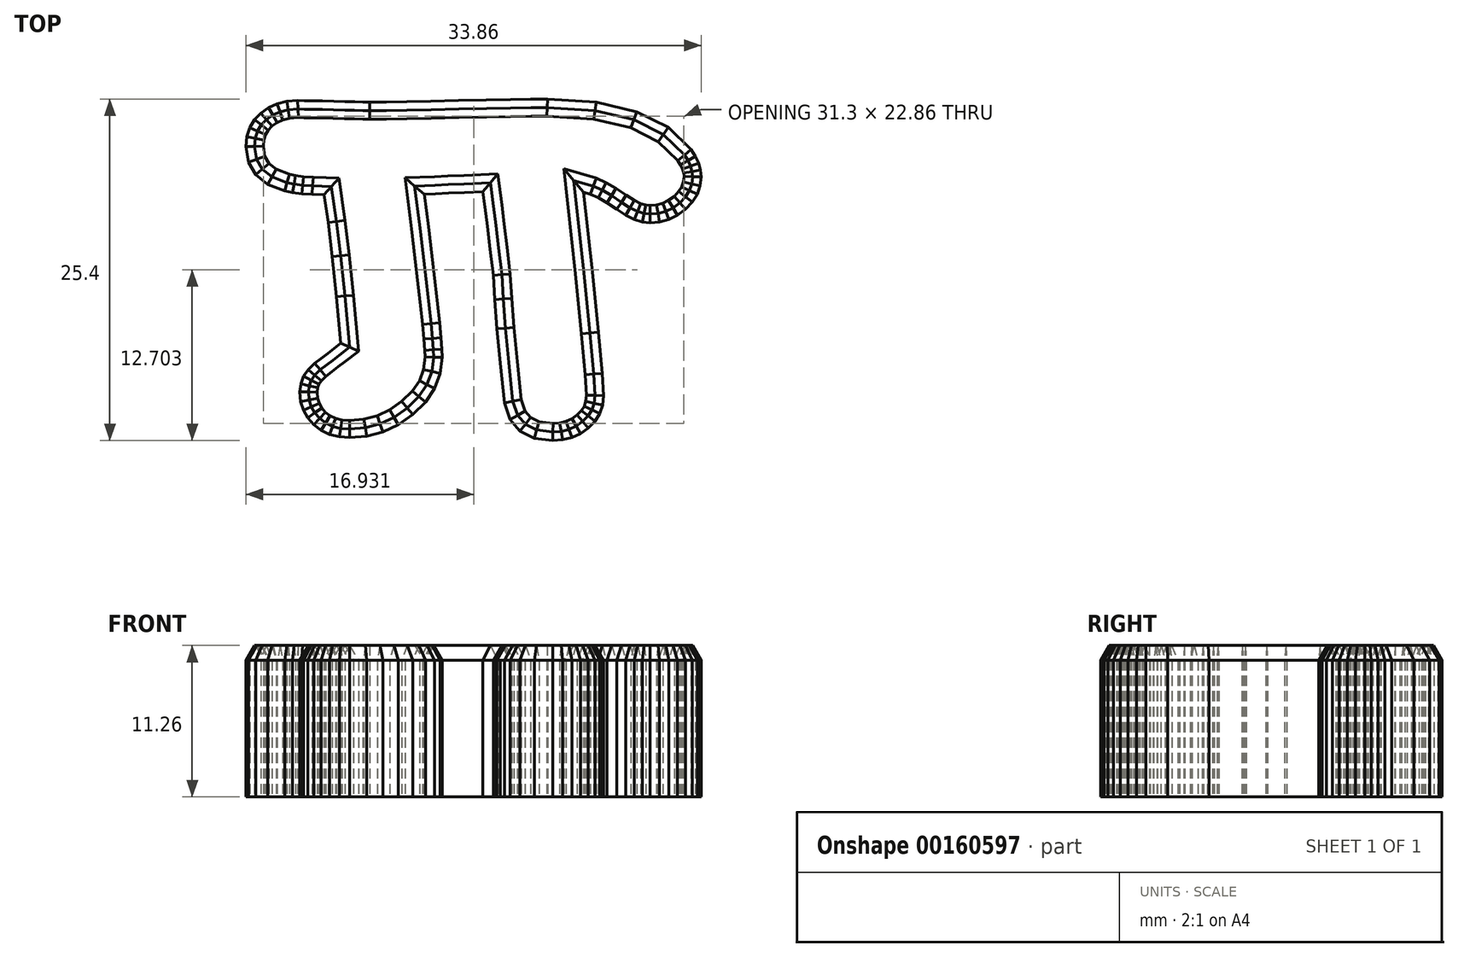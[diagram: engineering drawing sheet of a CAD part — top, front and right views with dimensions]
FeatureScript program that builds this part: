
annotation { "Feature Type Name" : "Feature", "Feature Type Description" : "" }
export const myFeature = defineFeature(function(context is Context, id is Id, definition is map)
    precondition{}
    {
        {
            var Q0;
            Q0=qCreatedBy(makeId("Top.planeOp"),FACE);
            var sketch = newSketch(context, id + "F0", { "sketchPlane" : qUnion([Q0])});
            skLineSegment(sketch, "E0", {"start": v(-14.06, 5.88) * mm, "end": v(-13.47, 5.76) * mm});
            skLineSegment(sketch, "E1", {"start": v(-13.47, 5.76) * mm, "end": v(-12.79, 5.67) * mm});
            skLineSegment(sketch, "E2", {"start": v(-12.79, 5.67) * mm, "end": v(-12, 5.6) * mm});
            skLineSegment(sketch, "E3", {"start": v(-12, 5.6) * mm, "end": v(-11.13, 5.58) * mm});
            skLineSegment(sketch, "E4", {"start": v(-11.13, 5.58) * mm, "end": v(-10.82, 3.51) * mm});
            skLineSegment(sketch, "E5", {"start": v(-10.82, 3.51) * mm, "end": v(-10.51, 0.98) * mm});
            skLineSegment(sketch, "E6", {"start": v(-10.51, 0.98) * mm, "end": v(-10.2, -2.01) * mm});
            skLineSegment(sketch, "E7", {"start": v(-10.2, -2.01) * mm, "end": v(-9.89, -5.47) * mm});
            skLineSegment(sketch, "E8", {"start": v(-9.89, -5.47) * mm, "end": v(-10.37, -5.84) * mm});
            skLineSegment(sketch, "E9", {"start": v(-10.37, -5.84) * mm, "end": v(-10.85, -6.21) * mm});
            skLineSegment(sketch, "E10", {"start": v(-10.85, -6.21) * mm, "end": v(-11.34, -6.59) * mm});
            skLineSegment(sketch, "E11", {"start": v(-11.34, -6.59) * mm, "end": v(-11.82, -6.96) * mm});
            skLineSegment(sketch, "E12", {"start": v(-11.82, -6.96) * mm, "end": v(-12.3, -7.41) * mm});
            skLineSegment(sketch, "E13", {"start": v(-12.3, -7.41) * mm, "end": v(-12.65, -7.92) * mm});
            skLineSegment(sketch, "E14", {"start": v(-12.65, -7.92) * mm, "end": v(-12.86, -8.48) * mm});
            skLineSegment(sketch, "E15", {"start": v(-12.86, -8.48) * mm, "end": v(-12.92, -9.09) * mm});
            skLineSegment(sketch, "E16", {"start": v(-12.92, -9.09) * mm, "end": v(-12.86, -9.8) * mm});
            skLineSegment(sketch, "E17", {"start": v(-12.86, -9.8) * mm, "end": v(-12.67, -10.44) * mm});
            skLineSegment(sketch, "E18", {"start": v(-12.67, -10.44) * mm, "end": v(-12.34, -11.02) * mm});
            skLineSegment(sketch, "E19", {"start": v(-12.34, -11.02) * mm, "end": v(-11.89, -11.53) * mm});
            skLineSegment(sketch, "E20", {"start": v(-11.89, -11.53) * mm, "end": v(-11.33, -11.95) * mm});
            skLineSegment(sketch, "E21", {"start": v(-11.33, -11.95) * mm, "end": v(-10.7, -12.24) * mm});
            skLineSegment(sketch, "E22", {"start": v(-10.7, -12.24) * mm, "end": v(-10, -12.42) * mm});
            skLineSegment(sketch, "E23", {"start": v(-10, -12.42) * mm, "end": v(-9.22, -12.48) * mm});
            skLineSegment(sketch, "E24", {"start": v(-9.22, -12.48) * mm, "end": v(-7.95, -12.38) * mm});
            skLineSegment(sketch, "E25", {"start": v(-7.95, -12.38) * mm, "end": v(-6.74, -12.05) * mm});
            skLineSegment(sketch, "E26", {"start": v(-6.74, -12.05) * mm, "end": v(-5.6, -11.52) * mm});
            skLineSegment(sketch, "E27", {"start": v(-5.6, -11.52) * mm, "end": v(-4.53, -10.77) * mm});
            skLineSegment(sketch, "E28", {"start": v(-4.53, -10.77) * mm, "end": v(-3.57, -9.84) * mm});
            skLineSegment(sketch, "E29", {"start": v(-3.57, -9.84) * mm, "end": v(-2.9, -8.82) * mm});
            skLineSegment(sketch, "E30", {"start": v(-2.9, -8.82) * mm, "end": v(-2.48, -7.72) * mm});
            skLineSegment(sketch, "E31", {"start": v(-2.48, -7.72) * mm, "end": v(-2.35, -6.52) * mm});
            skLineSegment(sketch, "E32", {"start": v(-2.35, -6.52) * mm, "end": v(-2.37, -5.92) * mm});
            skLineSegment(sketch, "E33", {"start": v(-2.37, -5.92) * mm, "end": v(-2.43, -5.05) * mm});
            skLineSegment(sketch, "E34", {"start": v(-2.43, -5.05) * mm, "end": v(-2.53, -3.93) * mm});
            skLineSegment(sketch, "E35", {"start": v(-2.53, -3.93) * mm, "end": v(-2.68, -2.54) * mm});
            skLineSegment(sketch, "E36", {"start": v(-2.68, -2.54) * mm, "end": v(-2.87, -0.9) * mm});
            skLineSegment(sketch, "E37", {"start": v(-2.87, -0.9) * mm, "end": v(-3.1, 1.02) * mm});
            skLineSegment(sketch, "E38", {"start": v(-3.1, 1.02) * mm, "end": v(-3.36, 3.2) * mm});
            skLineSegment(sketch, "E39", {"start": v(-3.36, 3.2) * mm, "end": v(-3.67, 5.63) * mm});
            skLineSegment(sketch, "E40", {"start": v(-3.67, 5.63) * mm, "end": v(-2.85, 5.67) * mm});
            skLineSegment(sketch, "E41", {"start": v(-2.85, 5.67) * mm, "end": v(-1.85, 5.7) * mm});
            skLineSegment(sketch, "E42", {"start": v(-1.85, 5.7) * mm, "end": v(-0.67, 5.76) * mm});
            skLineSegment(sketch, "E43", {"start": v(-0.67, 5.76) * mm, "end": v(0.7, 5.83) * mm});
            skLineSegment(sketch, "E44", {"start": v(0.7, 5.83) * mm, "end": v(0.84, 4.66) * mm});
            skLineSegment(sketch, "E45", {"start": v(0.84, 4.66) * mm, "end": v(1.02, 3.23) * mm});
            skLineSegment(sketch, "E46", {"start": v(1.02, 3.23) * mm, "end": v(1.23, 1.54) * mm});
            skLineSegment(sketch, "E47", {"start": v(1.23, 1.54) * mm, "end": v(1.46, -0.41) * mm});
            skLineSegment(sketch, "E48", {"start": v(1.46, -0.41) * mm, "end": v(1.57, -2.2) * mm});
            skLineSegment(sketch, "E49", {"start": v(1.57, -2.2) * mm, "end": v(1.74, -4.4) * mm});
            skLineSegment(sketch, "E50", {"start": v(1.74, -4.4) * mm, "end": v(1.98, -6.96) * mm});
            skLineSegment(sketch, "E51", {"start": v(1.98, -6.96) * mm, "end": v(2.3, -9.91) * mm});
            skLineSegment(sketch, "E52", {"start": v(2.3, -9.91) * mm, "end": v(2.71, -11.13) * mm});
            skLineSegment(sketch, "E53", {"start": v(2.71, -11.13) * mm, "end": v(3.45, -12) * mm});
            skLineSegment(sketch, "E54", {"start": v(3.45, -12) * mm, "end": v(4.5, -12.53) * mm});
            skLineSegment(sketch, "E55", {"start": v(4.5, -12.53) * mm, "end": v(5.88, -12.7) * mm});
            skLineSegment(sketch, "E56", {"start": v(5.88, -12.7) * mm, "end": v(6.62, -12.64) * mm});
            skLineSegment(sketch, "E57", {"start": v(6.62, -12.64) * mm, "end": v(7.3, -12.47) * mm});
            skLineSegment(sketch, "E58", {"start": v(7.3, -12.47) * mm, "end": v(7.94, -12.18) * mm});
            skLineSegment(sketch, "E59", {"start": v(7.94, -12.18) * mm, "end": v(8.53, -11.76) * mm});
            skLineSegment(sketch, "E60", {"start": v(8.53, -11.76) * mm, "end": v(9.03, -11.26) * mm});
            skLineSegment(sketch, "E61", {"start": v(9.03, -11.26) * mm, "end": v(9.38, -10.7) * mm});
            skLineSegment(sketch, "E62", {"start": v(9.38, -10.7) * mm, "end": v(9.6, -10.06) * mm});
            skLineSegment(sketch, "E63", {"start": v(9.6, -10.06) * mm, "end": v(9.67, -9.36) * mm});
            skLineSegment(sketch, "E64", {"start": v(9.67, -9.36) * mm, "end": v(9.57, -7.71) * mm});
            skLineSegment(sketch, "E65", {"start": v(9.57, -7.71) * mm, "end": v(9.3, -4.64) * mm});
            skLineSegment(sketch, "E66", {"start": v(9.3, -4.64) * mm, "end": v(8.83, -0.14) * mm});
            skLineSegment(sketch, "E67", {"start": v(8.83, -0.14) * mm, "end": v(8.17, 5.77) * mm});
            skLineSegment(sketch, "E68", {"start": v(8.17, 5.77) * mm, "end": v(8.7, 5.62) * mm});
            skLineSegment(sketch, "E69", {"start": v(8.7, 5.62) * mm, "end": v(9.28, 5.36) * mm});
            skLineSegment(sketch, "E70", {"start": v(9.28, 5.36) * mm, "end": v(9.93, 4.98) * mm});
            skLineSegment(sketch, "E71", {"start": v(9.93, 4.98) * mm, "end": v(10.66, 4.5) * mm});
            skLineSegment(sketch, "E72", {"start": v(10.66, 4.5) * mm, "end": v(11.33, 4.07) * mm});
            skLineSegment(sketch, "E73", {"start": v(11.33, 4.07) * mm, "end": v(11.96, 3.76) * mm});
            skLineSegment(sketch, "E74", {"start": v(11.96, 3.76) * mm, "end": v(12.56, 3.57) * mm});
            skLineSegment(sketch, "E75", {"start": v(12.56, 3.57) * mm, "end": v(13.12, 3.5) * mm});
            skLineSegment(sketch, "E76", {"start": v(13.12, 3.5) * mm, "end": v(13.84, 3.57) * mm});
            skLineSegment(sketch, "E77", {"start": v(13.84, 3.57) * mm, "end": v(14.53, 3.76) * mm});
            skLineSegment(sketch, "E78", {"start": v(14.53, 3.76) * mm, "end": v(15.17, 4.07) * mm});
            skLineSegment(sketch, "E79", {"start": v(15.17, 4.07) * mm, "end": v(15.77, 4.52) * mm});
            skLineSegment(sketch, "E80", {"start": v(15.77, 4.52) * mm, "end": v(16.28, 5.04) * mm});
            skLineSegment(sketch, "E81", {"start": v(16.28, 5.04) * mm, "end": v(16.64, 5.62) * mm});
            skLineSegment(sketch, "E82", {"start": v(16.64, 5.62) * mm, "end": v(16.86, 6.25) * mm});
            skLineSegment(sketch, "E83", {"start": v(16.86, 6.25) * mm, "end": v(16.93, 6.93) * mm});
            skLineSegment(sketch, "E84", {"start": v(16.93, 6.93) * mm, "end": v(16.88, 7.43) * mm});
            skLineSegment(sketch, "E85", {"start": v(16.88, 7.43) * mm, "end": v(16.74, 7.93) * mm});
            skLineSegment(sketch, "E86", {"start": v(16.74, 7.93) * mm, "end": v(16.5, 8.44) * mm});
            skLineSegment(sketch, "E87", {"start": v(16.5, 8.44) * mm, "end": v(16.18, 8.95) * mm});
            skLineSegment(sketch, "E88", {"start": v(16.18, 8.95) * mm, "end": v(14.48, 10.6) * mm});
            skLineSegment(sketch, "E89", {"start": v(14.48, 10.6) * mm, "end": v(12.13, 11.76) * mm});
            skLineSegment(sketch, "E90", {"start": v(12.13, 11.76) * mm, "end": v(9.14, 12.47) * mm});
            skLineSegment(sketch, "E91", {"start": v(9.14, 12.47) * mm, "end": v(5.5, 12.7) * mm});
            skLineSegment(sketch, "E92", {"start": v(5.5, 12.7) * mm, "end": v(4.25, 12.7) * mm});
            skLineSegment(sketch, "E93", {"start": v(4.25, 12.7) * mm, "end": v(2.74, 12.68) * mm});
            skLineSegment(sketch, "E94", {"start": v(2.74, 12.68) * mm, "end": v(0.95, 12.64) * mm});
            skLineSegment(sketch, "E95", {"start": v(0.95, 12.64) * mm, "end": v(-1.12, 12.6) * mm});
            skLineSegment(sketch, "E96", {"start": v(-1.12, 12.6) * mm, "end": v(-3.18, 12.54) * mm});
            skLineSegment(sketch, "E97", {"start": v(-3.18, 12.54) * mm, "end": v(-4.97, 12.51) * mm});
            skLineSegment(sketch, "E98", {"start": v(-4.97, 12.51) * mm, "end": v(-6.5, 12.49) * mm});
            skLineSegment(sketch, "E99", {"start": v(-6.5, 12.49) * mm, "end": v(-7.73, 12.48) * mm});
            skLineSegment(sketch, "E100", {"start": v(-7.73, 12.48) * mm, "end": v(-8.23, 12.49) * mm});
            skLineSegment(sketch, "E101", {"start": v(-8.23, 12.49) * mm, "end": v(-8.84, 12.5) * mm});
            skLineSegment(sketch, "E102", {"start": v(-8.84, 12.5) * mm, "end": v(-9.57, 12.51) * mm});
            skLineSegment(sketch, "E103", {"start": v(-9.57, 12.51) * mm, "end": v(-10.41, 12.54) * mm});
            skLineSegment(sketch, "E104", {"start": v(-10.41, 12.54) * mm, "end": v(-11.25, 12.56) * mm});
            skLineSegment(sketch, "E105", {"start": v(-11.25, 12.56) * mm, "end": v(-11.98, 12.58) * mm});
            skLineSegment(sketch, "E106", {"start": v(-11.98, 12.58) * mm, "end": v(-12.6, 12.59) * mm});
            skLineSegment(sketch, "E107", {"start": v(-12.6, 12.59) * mm, "end": v(-13.1, 12.6) * mm});
            skLineSegment(sketch, "E108", {"start": v(-13.1, 12.6) * mm, "end": v(-13.88, 12.54) * mm});
            skLineSegment(sketch, "E109", {"start": v(-13.88, 12.54) * mm, "end": v(-14.6, 12.36) * mm});
            skLineSegment(sketch, "E110", {"start": v(-14.6, 12.36) * mm, "end": v(-15.26, 12.07) * mm});
            skLineSegment(sketch, "E111", {"start": v(-15.26, 12.07) * mm, "end": v(-15.84, 11.67) * mm});
            skLineSegment(sketch, "E112", {"start": v(-15.84, 11.67) * mm, "end": v(-16.32, 11.16) * mm});
            skLineSegment(sketch, "E113", {"start": v(-16.32, 11.16) * mm, "end": v(-16.66, 10.58) * mm});
            skLineSegment(sketch, "E114", {"start": v(-16.66, 10.58) * mm, "end": v(-16.86, 9.92) * mm});
            skLineSegment(sketch, "E115", {"start": v(-16.86, 9.92) * mm, "end": v(-16.93, 9.17) * mm});
            skLineSegment(sketch, "E116", {"start": v(-16.93, 9.17) * mm, "end": v(-16.75, 8.01) * mm});
            skLineSegment(sketch, "E117", {"start": v(-16.75, 8.01) * mm, "end": v(-16.21, 7.08) * mm});
            skLineSegment(sketch, "E118", {"start": v(-16.21, 7.08) * mm, "end": v(-15.31, 6.37) * mm});
            skLineSegment(sketch, "E119", {"start": v(-15.31, 6.37) * mm, "end": v(-14.06, 5.88) * mm});
            skSolve(sketch);
        }
        {
            var Q0;
            Q0 = qSketchRegion(id + "F0", true);
            extrude(context, id + "F1", {"entities" : qUnion([Q0]), "depth" : 11.43 * mm});
        }
        {
            var Q0;
            Q0=makeQuery(id+"F1.opExtrude","CAP_FACE",FACE,{"disambiguationData":[OSD([sQuery(id+"F0.wireOp",EDGE,"E0"),sQuery(id+"F0.wireOp",EDGE,"E1"),sQuery(id+"F0.wireOp",EDGE,"E2"),sQuery(id+"F0.wireOp",EDGE,"E3"),sQuery(id+"F0.wireOp",EDGE,"E4"),sQuery(id+"F0.wireOp",EDGE,"E5"),sQuery(id+"F0.wireOp",EDGE,"E6"),sQuery(id+"F0.wireOp",EDGE,"E7"),sQuery(id+"F0.wireOp",EDGE,"E8"),sQuery(id+"F0.wireOp",EDGE,"E9"),sQuery(id+"F0.wireOp",EDGE,"E10"),sQuery(id+"F0.wireOp",EDGE,"E11"),sQuery(id+"F0.wireOp",EDGE,"E12"),sQuery(id+"F0.wireOp",EDGE,"E13"),sQuery(id+"F0.wireOp",EDGE,"E14"),sQuery(id+"F0.wireOp",EDGE,"E15"),sQuery(id+"F0.wireOp",EDGE,"E16"),sQuery(id+"F0.wireOp",EDGE,"E17"),sQuery(id+"F0.wireOp",EDGE,"E18"),sQuery(id+"F0.wireOp",EDGE,"E19"),sQuery(id+"F0.wireOp",EDGE,"E20"),sQuery(id+"F0.wireOp",EDGE,"E21"),sQuery(id+"F0.wireOp",EDGE,"E22"),sQuery(id+"F0.wireOp",EDGE,"E23"),sQuery(id+"F0.wireOp",EDGE,"E24"),sQuery(id+"F0.wireOp",EDGE,"E25"),sQuery(id+"F0.wireOp",EDGE,"E26"),sQuery(id+"F0.wireOp",EDGE,"E27"),sQuery(id+"F0.wireOp",EDGE,"E28"),sQuery(id+"F0.wireOp",EDGE,"E29"),sQuery(id+"F0.wireOp",EDGE,"E30"),sQuery(id+"F0.wireOp",EDGE,"E31"),sQuery(id+"F0.wireOp",EDGE,"E32"),sQuery(id+"F0.wireOp",EDGE,"E33"),sQuery(id+"F0.wireOp",EDGE,"E34"),sQuery(id+"F0.wireOp",EDGE,"E35"),sQuery(id+"F0.wireOp",EDGE,"E36"),sQuery(id+"F0.wireOp",EDGE,"E37"),sQuery(id+"F0.wireOp",EDGE,"E38"),sQuery(id+"F0.wireOp",EDGE,"E39"),sQuery(id+"F0.wireOp",EDGE,"E40"),sQuery(id+"F0.wireOp",EDGE,"E41"),sQuery(id+"F0.wireOp",EDGE,"E42"),sQuery(id+"F0.wireOp",EDGE,"E43"),sQuery(id+"F0.wireOp",EDGE,"E44"),sQuery(id+"F0.wireOp",EDGE,"E45"),sQuery(id+"F0.wireOp",EDGE,"E46"),sQuery(id+"F0.wireOp",EDGE,"E47"),sQuery(id+"F0.wireOp",EDGE,"E48"),sQuery(id+"F0.wireOp",EDGE,"E49"),sQuery(id+"F0.wireOp",EDGE,"E50"),sQuery(id+"F0.wireOp",EDGE,"E51"),sQuery(id+"F0.wireOp",EDGE,"E52"),sQuery(id+"F0.wireOp",EDGE,"E53"),sQuery(id+"F0.wireOp",EDGE,"E54"),sQuery(id+"F0.wireOp",EDGE,"E55"),sQuery(id+"F0.wireOp",EDGE,"E56"),sQuery(id+"F0.wireOp",EDGE,"E57"),sQuery(id+"F0.wireOp",EDGE,"E58"),sQuery(id+"F0.wireOp",EDGE,"E59"),sQuery(id+"F0.wireOp",EDGE,"E60"),sQuery(id+"F0.wireOp",EDGE,"E61"),sQuery(id+"F0.wireOp",EDGE,"E62"),sQuery(id+"F0.wireOp",EDGE,"E63"),sQuery(id+"F0.wireOp",EDGE,"E64"),sQuery(id+"F0.wireOp",EDGE,"E65"),sQuery(id+"F0.wireOp",EDGE,"E66"),sQuery(id+"F0.wireOp",EDGE,"E67"),sQuery(id+"F0.wireOp",EDGE,"E68"),sQuery(id+"F0.wireOp",EDGE,"E69"),sQuery(id+"F0.wireOp",EDGE,"E70"),sQuery(id+"F0.wireOp",EDGE,"E71"),sQuery(id+"F0.wireOp",EDGE,"E72"),sQuery(id+"F0.wireOp",EDGE,"E73"),sQuery(id+"F0.wireOp",EDGE,"E74"),sQuery(id+"F0.wireOp",EDGE,"E75"),sQuery(id+"F0.wireOp",EDGE,"E76"),sQuery(id+"F0.wireOp",EDGE,"E77"),sQuery(id+"F0.wireOp",EDGE,"E78"),sQuery(id+"F0.wireOp",EDGE,"E79"),sQuery(id+"F0.wireOp",EDGE,"E80"),sQuery(id+"F0.wireOp",EDGE,"E81"),sQuery(id+"F0.wireOp",EDGE,"E82"),sQuery(id+"F0.wireOp",EDGE,"E83"),sQuery(id+"F0.wireOp",EDGE,"E84"),sQuery(id+"F0.wireOp",EDGE,"E85"),sQuery(id+"F0.wireOp",EDGE,"E86"),sQuery(id+"F0.wireOp",EDGE,"E87"),sQuery(id+"F0.wireOp",EDGE,"E88"),sQuery(id+"F0.wireOp",EDGE,"E89"),sQuery(id+"F0.wireOp",EDGE,"E90"),sQuery(id+"F0.wireOp",EDGE,"E91"),sQuery(id+"F0.wireOp",EDGE,"E92"),sQuery(id+"F0.wireOp",EDGE,"E93"),sQuery(id+"F0.wireOp",EDGE,"E94"),sQuery(id+"F0.wireOp",EDGE,"E95"),sQuery(id+"F0.wireOp",EDGE,"E96"),sQuery(id+"F0.wireOp",EDGE,"E97"),sQuery(id+"F0.wireOp",EDGE,"E98"),sQuery(id+"F0.wireOp",EDGE,"E99"),sQuery(id+"F0.wireOp",EDGE,"E100"),sQuery(id+"F0.wireOp",EDGE,"E101"),sQuery(id+"F0.wireOp",EDGE,"E102"),sQuery(id+"F0.wireOp",EDGE,"E103"),sQuery(id+"F0.wireOp",EDGE,"E104"),sQuery(id+"F0.wireOp",EDGE,"E105"),sQuery(id+"F0.wireOp",EDGE,"E106"),sQuery(id+"F0.wireOp",EDGE,"E107"),sQuery(id+"F0.wireOp",EDGE,"E108"),sQuery(id+"F0.wireOp",EDGE,"E109"),sQuery(id+"F0.wireOp",EDGE,"E110"),sQuery(id+"F0.wireOp",EDGE,"E111"),sQuery(id+"F0.wireOp",EDGE,"E112"),sQuery(id+"F0.wireOp",EDGE,"E113"),sQuery(id+"F0.wireOp",EDGE,"E114"),sQuery(id+"F0.wireOp",EDGE,"E115"),sQuery(id+"F0.wireOp",EDGE,"E116"),sQuery(id+"F0.wireOp",EDGE,"E117"),sQuery(id+"F0.wireOp",EDGE,"E118"),sQuery(id+"F0.wireOp",EDGE,"E119")])],"isStart":false});
            shell(context, id + "F2", {"entities" : qUnion([Q0]), "thickness" : 1.27 * mm});
        }
        {
            var Q0;
            Q0=makeQuery(id+"F1.opExtrude","CAP_FACE",FACE,{"disambiguationData":[OSD([sQuery(id+"F0.wireOp",EDGE,"E0"),sQuery(id+"F0.wireOp",EDGE,"E1"),sQuery(id+"F0.wireOp",EDGE,"E2"),sQuery(id+"F0.wireOp",EDGE,"E3"),sQuery(id+"F0.wireOp",EDGE,"E4"),sQuery(id+"F0.wireOp",EDGE,"E5"),sQuery(id+"F0.wireOp",EDGE,"E6"),sQuery(id+"F0.wireOp",EDGE,"E7"),sQuery(id+"F0.wireOp",EDGE,"E8"),sQuery(id+"F0.wireOp",EDGE,"E9"),sQuery(id+"F0.wireOp",EDGE,"E10"),sQuery(id+"F0.wireOp",EDGE,"E11"),sQuery(id+"F0.wireOp",EDGE,"E12"),sQuery(id+"F0.wireOp",EDGE,"E13"),sQuery(id+"F0.wireOp",EDGE,"E14"),sQuery(id+"F0.wireOp",EDGE,"E15"),sQuery(id+"F0.wireOp",EDGE,"E16"),sQuery(id+"F0.wireOp",EDGE,"E17"),sQuery(id+"F0.wireOp",EDGE,"E18"),sQuery(id+"F0.wireOp",EDGE,"E19"),sQuery(id+"F0.wireOp",EDGE,"E20"),sQuery(id+"F0.wireOp",EDGE,"E21"),sQuery(id+"F0.wireOp",EDGE,"E22"),sQuery(id+"F0.wireOp",EDGE,"E23"),sQuery(id+"F0.wireOp",EDGE,"E24"),sQuery(id+"F0.wireOp",EDGE,"E25"),sQuery(id+"F0.wireOp",EDGE,"E26"),sQuery(id+"F0.wireOp",EDGE,"E27"),sQuery(id+"F0.wireOp",EDGE,"E28"),sQuery(id+"F0.wireOp",EDGE,"E29"),sQuery(id+"F0.wireOp",EDGE,"E30"),sQuery(id+"F0.wireOp",EDGE,"E31"),sQuery(id+"F0.wireOp",EDGE,"E32"),sQuery(id+"F0.wireOp",EDGE,"E33"),sQuery(id+"F0.wireOp",EDGE,"E34"),sQuery(id+"F0.wireOp",EDGE,"E35"),sQuery(id+"F0.wireOp",EDGE,"E36"),sQuery(id+"F0.wireOp",EDGE,"E37"),sQuery(id+"F0.wireOp",EDGE,"E38"),sQuery(id+"F0.wireOp",EDGE,"E39"),sQuery(id+"F0.wireOp",EDGE,"E40"),sQuery(id+"F0.wireOp",EDGE,"E41"),sQuery(id+"F0.wireOp",EDGE,"E42"),sQuery(id+"F0.wireOp",EDGE,"E43"),sQuery(id+"F0.wireOp",EDGE,"E44"),sQuery(id+"F0.wireOp",EDGE,"E45"),sQuery(id+"F0.wireOp",EDGE,"E46"),sQuery(id+"F0.wireOp",EDGE,"E47"),sQuery(id+"F0.wireOp",EDGE,"E48"),sQuery(id+"F0.wireOp",EDGE,"E49"),sQuery(id+"F0.wireOp",EDGE,"E50"),sQuery(id+"F0.wireOp",EDGE,"E51"),sQuery(id+"F0.wireOp",EDGE,"E52"),sQuery(id+"F0.wireOp",EDGE,"E53"),sQuery(id+"F0.wireOp",EDGE,"E54"),sQuery(id+"F0.wireOp",EDGE,"E55"),sQuery(id+"F0.wireOp",EDGE,"E56"),sQuery(id+"F0.wireOp",EDGE,"E57"),sQuery(id+"F0.wireOp",EDGE,"E58"),sQuery(id+"F0.wireOp",EDGE,"E59"),sQuery(id+"F0.wireOp",EDGE,"E60"),sQuery(id+"F0.wireOp",EDGE,"E61"),sQuery(id+"F0.wireOp",EDGE,"E62"),sQuery(id+"F0.wireOp",EDGE,"E63"),sQuery(id+"F0.wireOp",EDGE,"E64"),sQuery(id+"F0.wireOp",EDGE,"E65"),sQuery(id+"F0.wireOp",EDGE,"E66"),sQuery(id+"F0.wireOp",EDGE,"E67"),sQuery(id+"F0.wireOp",EDGE,"E68"),sQuery(id+"F0.wireOp",EDGE,"E69"),sQuery(id+"F0.wireOp",EDGE,"E70"),sQuery(id+"F0.wireOp",EDGE,"E71"),sQuery(id+"F0.wireOp",EDGE,"E72"),sQuery(id+"F0.wireOp",EDGE,"E73"),sQuery(id+"F0.wireOp",EDGE,"E74"),sQuery(id+"F0.wireOp",EDGE,"E75"),sQuery(id+"F0.wireOp",EDGE,"E76"),sQuery(id+"F0.wireOp",EDGE,"E77"),sQuery(id+"F0.wireOp",EDGE,"E78"),sQuery(id+"F0.wireOp",EDGE,"E79"),sQuery(id+"F0.wireOp",EDGE,"E80"),sQuery(id+"F0.wireOp",EDGE,"E81"),sQuery(id+"F0.wireOp",EDGE,"E82"),sQuery(id+"F0.wireOp",EDGE,"E83"),sQuery(id+"F0.wireOp",EDGE,"E84"),sQuery(id+"F0.wireOp",EDGE,"E85"),sQuery(id+"F0.wireOp",EDGE,"E86"),sQuery(id+"F0.wireOp",EDGE,"E87"),sQuery(id+"F0.wireOp",EDGE,"E88"),sQuery(id+"F0.wireOp",EDGE,"E89"),sQuery(id+"F0.wireOp",EDGE,"E90"),sQuery(id+"F0.wireOp",EDGE,"E91"),sQuery(id+"F0.wireOp",EDGE,"E92"),sQuery(id+"F0.wireOp",EDGE,"E93"),sQuery(id+"F0.wireOp",EDGE,"E94"),sQuery(id+"F0.wireOp",EDGE,"E95"),sQuery(id+"F0.wireOp",EDGE,"E96"),sQuery(id+"F0.wireOp",EDGE,"E97"),sQuery(id+"F0.wireOp",EDGE,"E98"),sQuery(id+"F0.wireOp",EDGE,"E99"),sQuery(id+"F0.wireOp",EDGE,"E100"),sQuery(id+"F0.wireOp",EDGE,"E101"),sQuery(id+"F0.wireOp",EDGE,"E102"),sQuery(id+"F0.wireOp",EDGE,"E103"),sQuery(id+"F0.wireOp",EDGE,"E104"),sQuery(id+"F0.wireOp",EDGE,"E105"),sQuery(id+"F0.wireOp",EDGE,"E106"),sQuery(id+"F0.wireOp",EDGE,"E107"),sQuery(id+"F0.wireOp",EDGE,"E108"),sQuery(id+"F0.wireOp",EDGE,"E109"),sQuery(id+"F0.wireOp",EDGE,"E110"),sQuery(id+"F0.wireOp",EDGE,"E111"),sQuery(id+"F0.wireOp",EDGE,"E112"),sQuery(id+"F0.wireOp",EDGE,"E113"),sQuery(id+"F0.wireOp",EDGE,"E114"),sQuery(id+"F0.wireOp",EDGE,"E115"),sQuery(id+"F0.wireOp",EDGE,"E116"),sQuery(id+"F0.wireOp",EDGE,"E117"),sQuery(id+"F0.wireOp",EDGE,"E118"),sQuery(id+"F0.wireOp",EDGE,"E119")])],"isStart":true});
            extrude(context, id + "F3", {"entities" : qUnion([Q0]), "operationType" : NewBodyOperationType.REMOVE, "oppositeDirection" : true, "depth" : 1.27 * mm});
        }
        {
            var Q0;
            Q0=makeQuery(id+"F1.opExtrude","CAP_FACE",FACE,{"disambiguationData":[OSD([sQuery(id+"F0.wireOp",EDGE,"E0"),sQuery(id+"F0.wireOp",EDGE,"E1"),sQuery(id+"F0.wireOp",EDGE,"E2"),sQuery(id+"F0.wireOp",EDGE,"E3"),sQuery(id+"F0.wireOp",EDGE,"E4"),sQuery(id+"F0.wireOp",EDGE,"E5"),sQuery(id+"F0.wireOp",EDGE,"E6"),sQuery(id+"F0.wireOp",EDGE,"E7"),sQuery(id+"F0.wireOp",EDGE,"E8"),sQuery(id+"F0.wireOp",EDGE,"E9"),sQuery(id+"F0.wireOp",EDGE,"E10"),sQuery(id+"F0.wireOp",EDGE,"E11"),sQuery(id+"F0.wireOp",EDGE,"E12"),sQuery(id+"F0.wireOp",EDGE,"E13"),sQuery(id+"F0.wireOp",EDGE,"E14"),sQuery(id+"F0.wireOp",EDGE,"E15"),sQuery(id+"F0.wireOp",EDGE,"E16"),sQuery(id+"F0.wireOp",EDGE,"E17"),sQuery(id+"F0.wireOp",EDGE,"E18"),sQuery(id+"F0.wireOp",EDGE,"E19"),sQuery(id+"F0.wireOp",EDGE,"E20"),sQuery(id+"F0.wireOp",EDGE,"E21"),sQuery(id+"F0.wireOp",EDGE,"E22"),sQuery(id+"F0.wireOp",EDGE,"E23"),sQuery(id+"F0.wireOp",EDGE,"E24"),sQuery(id+"F0.wireOp",EDGE,"E25"),sQuery(id+"F0.wireOp",EDGE,"E26"),sQuery(id+"F0.wireOp",EDGE,"E27"),sQuery(id+"F0.wireOp",EDGE,"E28"),sQuery(id+"F0.wireOp",EDGE,"E29"),sQuery(id+"F0.wireOp",EDGE,"E30"),sQuery(id+"F0.wireOp",EDGE,"E31"),sQuery(id+"F0.wireOp",EDGE,"E32"),sQuery(id+"F0.wireOp",EDGE,"E33"),sQuery(id+"F0.wireOp",EDGE,"E34"),sQuery(id+"F0.wireOp",EDGE,"E35"),sQuery(id+"F0.wireOp",EDGE,"E36"),sQuery(id+"F0.wireOp",EDGE,"E37"),sQuery(id+"F0.wireOp",EDGE,"E38"),sQuery(id+"F0.wireOp",EDGE,"E39"),sQuery(id+"F0.wireOp",EDGE,"E40"),sQuery(id+"F0.wireOp",EDGE,"E41"),sQuery(id+"F0.wireOp",EDGE,"E42"),sQuery(id+"F0.wireOp",EDGE,"E43"),sQuery(id+"F0.wireOp",EDGE,"E44"),sQuery(id+"F0.wireOp",EDGE,"E45"),sQuery(id+"F0.wireOp",EDGE,"E46"),sQuery(id+"F0.wireOp",EDGE,"E47"),sQuery(id+"F0.wireOp",EDGE,"E48"),sQuery(id+"F0.wireOp",EDGE,"E49"),sQuery(id+"F0.wireOp",EDGE,"E50"),sQuery(id+"F0.wireOp",EDGE,"E51"),sQuery(id+"F0.wireOp",EDGE,"E52"),sQuery(id+"F0.wireOp",EDGE,"E53"),sQuery(id+"F0.wireOp",EDGE,"E54"),sQuery(id+"F0.wireOp",EDGE,"E55"),sQuery(id+"F0.wireOp",EDGE,"E56"),sQuery(id+"F0.wireOp",EDGE,"E57"),sQuery(id+"F0.wireOp",EDGE,"E58"),sQuery(id+"F0.wireOp",EDGE,"E59"),sQuery(id+"F0.wireOp",EDGE,"E60"),sQuery(id+"F0.wireOp",EDGE,"E61"),sQuery(id+"F0.wireOp",EDGE,"E62"),sQuery(id+"F0.wireOp",EDGE,"E63"),sQuery(id+"F0.wireOp",EDGE,"E64"),sQuery(id+"F0.wireOp",EDGE,"E65"),sQuery(id+"F0.wireOp",EDGE,"E66"),sQuery(id+"F0.wireOp",EDGE,"E67"),sQuery(id+"F0.wireOp",EDGE,"E68"),sQuery(id+"F0.wireOp",EDGE,"E69"),sQuery(id+"F0.wireOp",EDGE,"E70"),sQuery(id+"F0.wireOp",EDGE,"E71"),sQuery(id+"F0.wireOp",EDGE,"E72"),sQuery(id+"F0.wireOp",EDGE,"E73"),sQuery(id+"F0.wireOp",EDGE,"E74"),sQuery(id+"F0.wireOp",EDGE,"E75"),sQuery(id+"F0.wireOp",EDGE,"E76"),sQuery(id+"F0.wireOp",EDGE,"E77"),sQuery(id+"F0.wireOp",EDGE,"E78"),sQuery(id+"F0.wireOp",EDGE,"E79"),sQuery(id+"F0.wireOp",EDGE,"E80"),sQuery(id+"F0.wireOp",EDGE,"E81"),sQuery(id+"F0.wireOp",EDGE,"E82"),sQuery(id+"F0.wireOp",EDGE,"E83"),sQuery(id+"F0.wireOp",EDGE,"E84"),sQuery(id+"F0.wireOp",EDGE,"E85"),sQuery(id+"F0.wireOp",EDGE,"E86"),sQuery(id+"F0.wireOp",EDGE,"E87"),sQuery(id+"F0.wireOp",EDGE,"E88"),sQuery(id+"F0.wireOp",EDGE,"E89"),sQuery(id+"F0.wireOp",EDGE,"E90"),sQuery(id+"F0.wireOp",EDGE,"E91"),sQuery(id+"F0.wireOp",EDGE,"E92"),sQuery(id+"F0.wireOp",EDGE,"E93"),sQuery(id+"F0.wireOp",EDGE,"E94"),sQuery(id+"F0.wireOp",EDGE,"E95"),sQuery(id+"F0.wireOp",EDGE,"E96"),sQuery(id+"F0.wireOp",EDGE,"E97"),sQuery(id+"F0.wireOp",EDGE,"E98"),sQuery(id+"F0.wireOp",EDGE,"E99"),sQuery(id+"F0.wireOp",EDGE,"E100"),sQuery(id+"F0.wireOp",EDGE,"E101"),sQuery(id+"F0.wireOp",EDGE,"E102"),sQuery(id+"F0.wireOp",EDGE,"E103"),sQuery(id+"F0.wireOp",EDGE,"E104"),sQuery(id+"F0.wireOp",EDGE,"E105"),sQuery(id+"F0.wireOp",EDGE,"E106"),sQuery(id+"F0.wireOp",EDGE,"E107"),sQuery(id+"F0.wireOp",EDGE,"E108"),sQuery(id+"F0.wireOp",EDGE,"E109"),sQuery(id+"F0.wireOp",EDGE,"E110"),sQuery(id+"F0.wireOp",EDGE,"E111"),sQuery(id+"F0.wireOp",EDGE,"E112"),sQuery(id+"F0.wireOp",EDGE,"E113"),sQuery(id+"F0.wireOp",EDGE,"E114"),sQuery(id+"F0.wireOp",EDGE,"E115"),sQuery(id+"F0.wireOp",EDGE,"E116"),sQuery(id+"F0.wireOp",EDGE,"E117"),sQuery(id+"F0.wireOp",EDGE,"E118"),sQuery(id+"F0.wireOp",EDGE,"E119")])],"isStart":false});
            extrude(context, id + "F4", {"entities" : qUnion([Q0]), "depth" : 2.54 * mm, "hasDraft" : true, "draftAngle" : 30 * degree, "draftPullDirection" : true});
        }
    });
